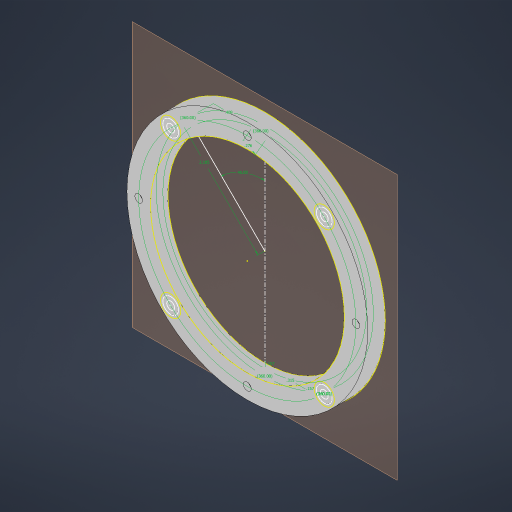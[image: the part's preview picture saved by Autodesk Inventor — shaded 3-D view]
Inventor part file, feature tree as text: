
AUTODESK INVENTOR PART (.ipt)
format: ipt  version: 2024 (Build 280153000, 153)  size: 265,728 bytes
history: native  units: in
note: dims shown in document units (in); Inventor stores cm internally (conversion verified against a paired STEP export)
features: extrude x5, other x4, sketch x2, plane x1, reference x1
ambient origin geometry x8: Origin, YZ Plane, XZ Plane, XY Plane, X Axis, Y Axis, Z Axis, Center Point
bodies: Solid1 (feature_tree)
feature tree (13):
  plane  "Work Plane1"
  sketch  "Sketch1"  dims[d0=0.35in d1=0.0in d2=0.2756in]
  extrude  "Extrusion1"  Depth=0.2756in
  extrude  "Extrusion2"  Depth=0.25in TaperAngle=0.0deg
  sketch  "Sketch2"  dims[d3=1.5748in d5=360.0deg d7=0.25in d8=0.0in d10=1.5748in d11=45.0deg d12=0.409in d13=2.185in d14=1.5748in d16=360.0deg d18=0.315in d19=1.5748in d21=360.0deg d23=0.25in d24=0.0in d25=0.1575in d26=1.5748in d28=360.0deg d30=0.625in d31=0.0in d32=0.1575in d33=1.5748in d35=360.0deg d37=0.0in d38=0.0in]
  extrude  "Extrusion3"  Depth=0.1575in
  extrude  "Extrusion4"  TaperAngle=45.0deg  [1 undecoded]
  extrude  "Extrusion5"  Depth=0.1575in
  reference  "Reference1"
  other  "<userpath>\CodingProjects\C-AAM\CAD\V1\Base.iam"
  other  "Base.iam"
  other  "LazySusan:1"
  other  "IR:1"
note: 1 required parameter value undecoded (feature->parameter linkage not recoverable at this tier; creation-order binding heuristic only, values carry confidence <= 0.55)
